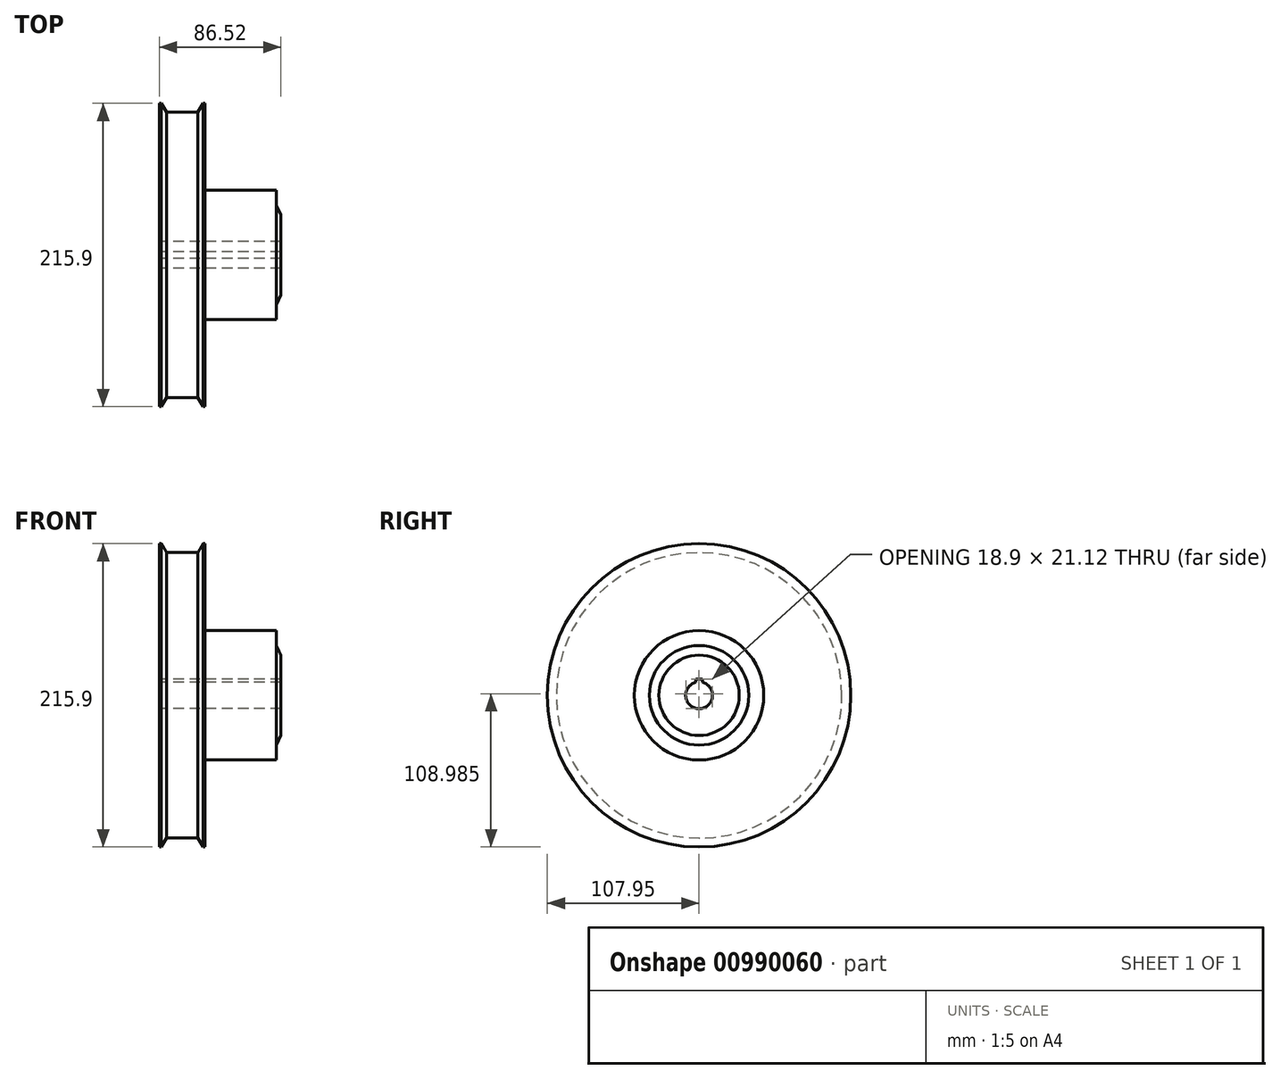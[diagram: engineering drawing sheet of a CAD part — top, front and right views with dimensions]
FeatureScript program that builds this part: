
annotation { "Feature Type Name" : "Feature", "Feature Type Description" : "" }
export const myFeature = defineFeature(function(context is Context, id is Id, definition is map)
    precondition{}
    {
        {
            var Q0;
            Q0=qCreatedBy(makeId("Front.planeOp"),FACE);
            var sketch = newSketch(context, id + "F0", { "sketchPlane" : qUnion([Q0])});
            skLineSegment(sketch, "E0", {"start": v(0, 0) * mm, "end": v(86.52, 0) * mm, "construction": true});
            skLineSegment(sketch, "E1", {"start": v(0, 9.52) * mm, "end": v(0, 107.95) * mm});
            skLineSegment(sketch, "E2", {"start": v(0, 107.95) * mm, "end": v(1.5, 107.95) * mm});
            skLineSegment(sketch, "E3", {"start": v(1.5, 107.95) * mm, "end": v(5.16, 101.6) * mm});
            skLineSegment(sketch, "E4", {"start": v(5.16, 101.6) * mm, "end": v(27.38, 101.6) * mm});
            skLineSegment(sketch, "E5", {"start": v(27.38, 101.6) * mm, "end": v(31.05, 107.95) * mm});
            skLineSegment(sketch, "E6", {"start": v(31.05, 107.95) * mm, "end": v(32.54, 107.95) * mm});
            skLineSegment(sketch, "E7", {"start": v(32.54, 107.95) * mm, "end": v(32.54, 46.04) * mm});
            skLineSegment(sketch, "E8", {"start": v(32.54, 46.04) * mm, "end": v(83.34, 46.04) * mm});
            skLineSegment(sketch, "E9", {"start": v(83.34, 46.04) * mm, "end": v(83.34, 35.38) * mm});
            skLineSegment(sketch, "E10", {"start": v(83.34, 35.38) * mm, "end": v(86.52, 28.57) * mm});
            skLineSegment(sketch, "E11", {"start": v(86.52, 28.58) * mm, "end": v(86.52, 9.53) * mm});
            skLineSegment(sketch, "E12", {"start": v(0, 9.53) * mm, "end": v(86.52, 9.53) * mm});
            skSolve(sketch);
        }
        {
            var Q0;
            Q0=makeQuery(id+"F0.imprint","IMPRINT",FACE,{"disambiguationData":[TD([[makeQuery(id+"F0.imprint","IMPRINT",EDGE,{"derivedFrom":sQuery(id+"F0.wireOp",EDGE,"E1")}),-1.0]])]});
            var Q1;
            Q1=sQuery(id+"F0.wireOp",EDGE,"E0");
            revolve(context, id + "F1", {"surfaceOperationType" : NewSurfaceOperationType.NEW, "entities" : qUnion([Q0]), "axis" : qUnion([Q1]), "revolveType" : RevolveType.FULL});
        }
        {
            var Q0;
            Q0=qCreatedBy(makeId("Right.planeOp"),FACE);
            var sketch = newSketch(context, id + "F2", { "sketchPlane" : qUnion([Q0])});
            skCircle(sketch, "E13.0", {"center": v(0, 0) * mm, "radius": 9.53 * mm, "construction": true});
            skLineSegment(sketch, "E14.bottom", {"start": v(2.38, 6.83) * mm, "end": v(-2.38, 6.83) * mm});
            skLineSegment(sketch, "E14.top", {"start": v(2.38, 11.6) * mm, "end": v(-2.38, 11.6) * mm});
            skLineSegment(sketch, "E14.left", {"start": v(2.38, 6.83) * mm, "end": v(2.38, 11.6) * mm});
            skLineSegment(sketch, "E14.right", {"start": v(-2.38, 6.83) * mm, "end": v(-2.38, 11.6) * mm});
            skPoint(sketch, "E15", {"position": v(0, 9.52) * mm});
            skLineSegment(sketch, "E16", {"start": v(0, 6.83) * mm, "end": v(0, 0) * mm, "construction": true});
            skSolve(sketch);
        }
        {
            var Q0;
            Q0 = qSketchRegion(id + "F2", true);
            extrude(context, id + "F3", {"entities" : qUnion([Q0]), "operationType" : NewBodyOperationType.REMOVE, "endBound" : BoundingType.THROUGH_ALL, "depth" : 25.4 * mm, "offsetDistance" : 25.4 * mm});
        }
    });
